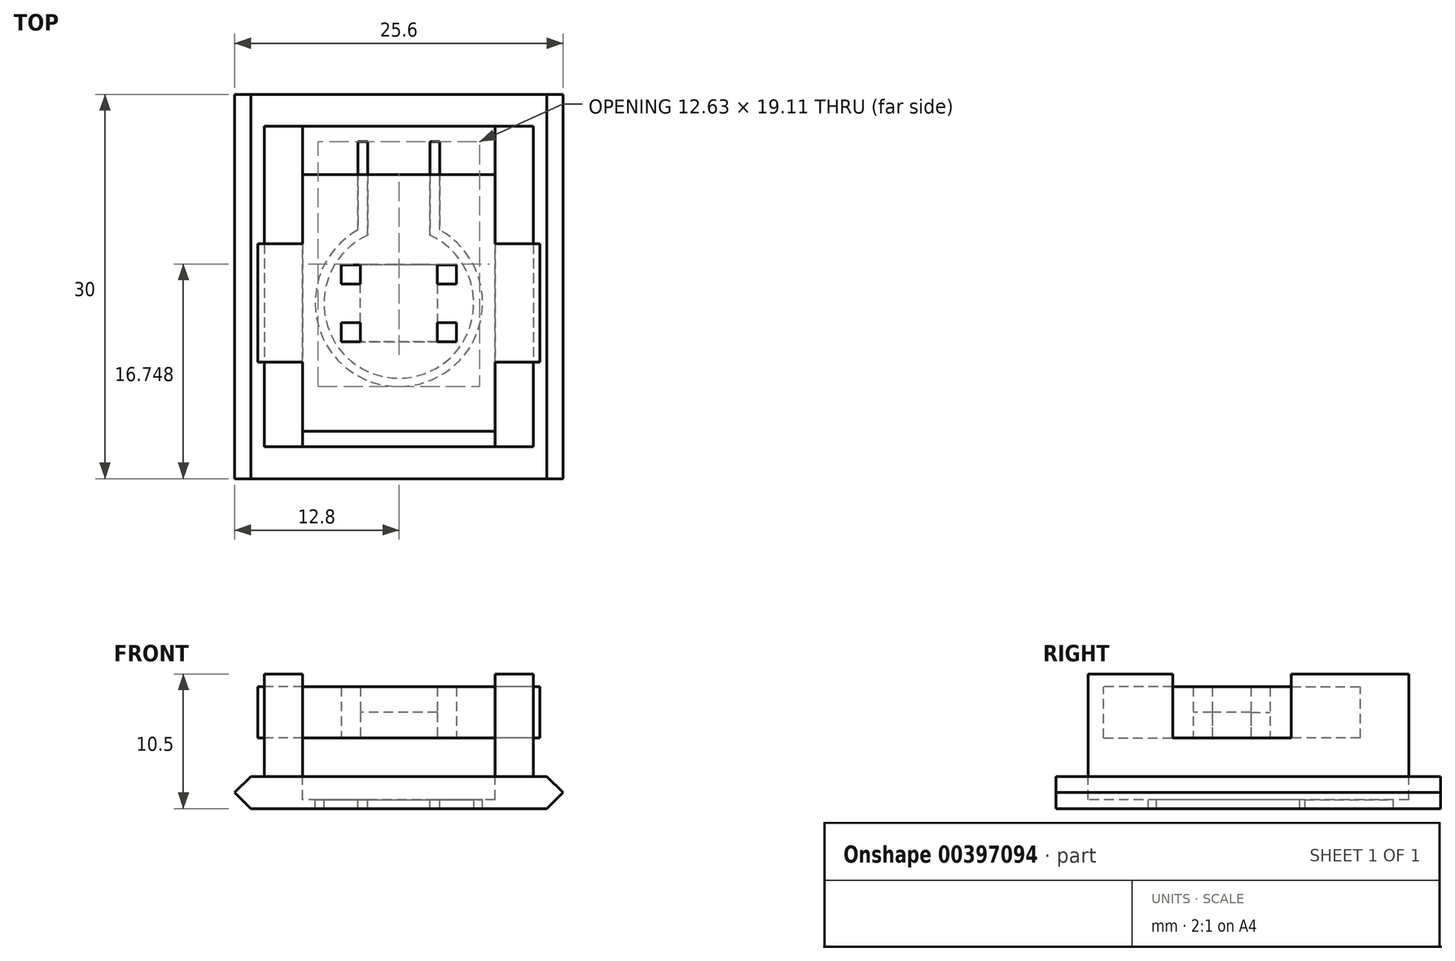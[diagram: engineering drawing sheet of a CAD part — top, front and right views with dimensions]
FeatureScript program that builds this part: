
annotation { "Feature Type Name" : "Feature", "Feature Type Description" : "" }
export const myFeature = defineFeature(function(context is Context, id is Id, definition is map)
    precondition{}
    {
        {
            var Q0;
            Q0=qCreatedBy(makeId("Front.planeOp"),FACE);
            var sketch = newSketch(context, id + "F0", { "sketchPlane" : qUnion([Q0])});
            skLineSegment(sketch, "E0", {"start": v(-11.55, 1.25) * mm, "end": v(11.55, 1.25) * mm});
            skLineSegment(sketch, "E1", {"start": v(11.55, -1.25) * mm, "end": v(-11.55, -1.25) * mm});
            skLineSegment(sketch, "E2", {"start": v(11.55, 1.25) * mm, "end": v(11.55, -1.25) * mm, "construction": true});
            skLineSegment(sketch, "E3", {"start": v(11.55, 1.25) * mm, "end": v(12.8, 0) * mm});
            skLineSegment(sketch, "E4", {"start": v(12.8, 0) * mm, "end": v(11.55, -1.25) * mm});
            skLineSegment(sketch, "E5", {"start": v(-11.55, 1.25) * mm, "end": v(-12.8, 0) * mm});
            skLineSegment(sketch, "E6", {"start": v(-12.8, 0) * mm, "end": v(-11.55, -1.25) * mm});
            skSolve(sketch);
        }
        {
            var Q0;
            Q0=qSketchRegion(id+"F0",true);
            extrude(context, id + "F1", {"entities" : qUnion([Q0]), "depth" : 30 * mm});
        }
        {
            var Q0;
            Q0=makeQuery(id+"F1.opExtrude","SWEPT_FACE",FACE,{"disambiguationData":[OSD([sQuery(id+"F0.wireOp",EDGE,"E0")])]});
            var sketch = newSketch(context, id + "F2", { "sketchPlane" : qUnion([Q0])});
            skLineSegment(sketch, "E7.bottom", {"start": v(7.5, -2.5) * mm, "end": v(-7.5, -2.5) * mm});
            skLineSegment(sketch, "E7.top", {"start": v(7.5, -27.5) * mm, "end": v(-7.5, -27.5) * mm});
            skLineSegment(sketch, "E7.left", {"start": v(7.5, -2.5) * mm, "end": v(7.5, -27.5) * mm});
            skLineSegment(sketch, "E7.right", {"start": v(-7.5, -2.5) * mm, "end": v(-7.5, -27.5) * mm});
            skPoint(sketch, "E7.middle", {"position": v(0, -15) * mm});
            skLineSegment(sketch, "E8", {"start": v(0, 0) * mm, "end": v(0, -30) * mm, "construction": true});
            skSolve(sketch);
        }
        {
            var Q0;
            Q0=qSketchRegion(id+"F2",true);
            extrude(context, id + "F3", {"entities" : qUnion([Q0]), "operationType" : NewBodyOperationType.REMOVE, "oppositeDirection" : true, "depth" : 1.8 * mm});
        }
        {
            var Q0;
            Q0=makeQuery(id+"F3.boolean.opBoolean","COPY",FACE,{"derivedFrom":makeQuery(id+"F3.opExtrude","CAP_FACE",FACE,{"disambiguationData":[OSD([sQuery(id+"F2.wireOp",EDGE,"E7.bottom"),sQuery(id+"F2.wireOp",EDGE,"E7.top"),sQuery(id+"F2.wireOp",EDGE,"E7.left"),sQuery(id+"F2.wireOp",EDGE,"E7.right")])],"isStart":false})});
            var sketch = newSketch(context, id + "F4", { "sketchPlane" : qUnion([Q0])});
            skLineSegment(sketch, "E9", {"start": v(-3.2, -10.59) * mm, "end": v(-3.2, -3.7) * mm});
            skLineSegment(sketch, "E10", {"start": v(-3.2, -3.7) * mm, "end": v(-2.43, -3.7) * mm});
            skLineSegment(sketch, "E11", {"start": v(-2.43, -3.7) * mm, "end": v(-2.43, -11) * mm});
            skLineSegment(sketch, "E12", {"start": v(0, -2.5) * mm, "end": v(0, -27.5) * mm, "construction": true});
            skLineSegment(sketch, "E13.MirrorCS", {"start": v(2.43, -3.7) * mm, "end": v(2.43, -11) * mm});
            skLineSegment(sketch, "E14.MirrorCS", {"start": v(3.2, -3.7) * mm, "end": v(2.43, -3.7) * mm});
            skLineSegment(sketch, "E15.MirrorCS", {"start": v(3.2, -10.59) * mm, "end": v(3.2, -3.7) * mm});
            skArc(sketch, "E16", {"start": v(-3.2, -10.59) * mm, "mid": v(0, -22.8) * mm, "end": v(3.2, -10.59) * mm});
            skArc(sketch, "E17", {"start": v(-2.43, -11) * mm, "mid": v(0, -22.15) * mm, "end": v(2.43, -11) * mm});
            skSolve(sketch);
        }
        {
            var Q0;
            Q0=qSketchRegion(id+"F4",true);
            extrude(context, id + "F5", {"entities" : qUnion([Q0]), "operationType" : NewBodyOperationType.REMOVE, "oppositeDirection" : true, "depth" : 25 * mm});
        }
        {
            var Q0;
            Q0=makeQuery(id+"F1.opExtrude","SWEPT_FACE",FACE,{"disambiguationData":[OSD([sQuery(id+"F0.wireOp",EDGE,"E0")])]});
            var sketch = newSketch(context, id + "F6", { "sketchPlane" : qUnion([Q0])});
            skLineSegment(sketch, "E18.bottom", {"start": v(-7.5, -2.5) * mm, "end": v(-10.5, -2.5) * mm});
            skLineSegment(sketch, "E18.top", {"start": v(-7.5, -27.5) * mm, "end": v(-10.5, -27.5) * mm});
            skLineSegment(sketch, "E18.left", {"start": v(-7.5, -2.5) * mm, "end": v(-7.5, -27.5) * mm});
            skLineSegment(sketch, "E18.right", {"start": v(-10.5, -2.5) * mm, "end": v(-10.5, -27.5) * mm});
            skLineSegment(sketch, "E19.bottom", {"start": v(7.5, -2.5) * mm, "end": v(10.5, -2.5) * mm});
            skLineSegment(sketch, "E19.top", {"start": v(7.5, -27.5) * mm, "end": v(10.5, -27.5) * mm});
            skLineSegment(sketch, "E19.left", {"start": v(7.5, -2.5) * mm, "end": v(7.5, -27.5) * mm});
            skLineSegment(sketch, "E19.right", {"start": v(10.5, -2.5) * mm, "end": v(10.5, -27.5) * mm});
            skSolve(sketch);
        }
        {
            var Q0;
            Q0=qSketchRegion(id+"F6",true);
            extrude(context, id + "F7", {"entities" : qUnion([Q0]), "operationType" : NewBodyOperationType.ADD, "depth" : 8 * mm});
        }
        {
            var Q0;
            Q0=makeQuery(id+"F7.opExtrude","CAP_FACE",FACE,{"disambiguationData":[OSD([sQuery(id+"F6.wireOp",EDGE,"E18.bottom"),sQuery(id+"F6.wireOp",EDGE,"E18.top"),sQuery(id+"F6.wireOp",EDGE,"E18.left"),sQuery(id+"F6.wireOp",EDGE,"E18.right")])],"isStart":false});
            var sketch = newSketch(context, id + "F8", { "sketchPlane" : qUnion([Q0])});
            skPoint(sketch, "E20.0", {"position": v(0, -27.5) * mm});
            skPoint(sketch, "E21.0", {"position": v(0, -2.5) * mm});
            skPoint(sketch, "E22.0", {"position": v(-7.5, -15) * mm});
            skArc(sketch, "E23.0", {"start": v(-3.2, -10.59) * mm, "mid": v(0, -22.8) * mm, "end": v(3.2, -10.59) * mm, "construction": true});
            skLineSegment(sketch, "E24.bottom", {"start": v(11, -20.9) * mm, "end": v(-11, -20.9) * mm});
            skLineSegment(sketch, "E24.top", {"start": v(11, -11.66) * mm, "end": v(-11, -11.66) * mm});
            skLineSegment(sketch, "E24.left", {"start": v(11, -20.9) * mm, "end": v(11, -11.66) * mm});
            skLineSegment(sketch, "E24.right", {"start": v(-11, -20.9) * mm, "end": v(-11, -11.66) * mm});
            skLineSegment(sketch, "E25.0", {"start": v(7.5, -2.5) * mm, "end": v(7.5, -27.5) * mm, "construction": true});
            skLineSegment(sketch, "E26.0", {"start": v(-7.5, -2.5) * mm, "end": v(-7.5, -27.5) * mm, "construction": true});
            skLineSegment(sketch, "E27.bottom", {"start": v(7.5, -26.3) * mm, "end": v(-7.5, -26.3) * mm});
            skLineSegment(sketch, "E27.top", {"start": v(7.5, -6.26) * mm, "end": v(-7.5, -6.26) * mm});
            skLineSegment(sketch, "E27.left", {"start": v(7.5, -26.3) * mm, "end": v(7.5, -6.26) * mm});
            skLineSegment(sketch, "E27.right", {"start": v(-7.5, -26.3) * mm, "end": v(-7.5, -6.26) * mm});
            skSolve(sketch);
        }
        {
            var Q0;
            Q0=qSketchRegion(id+"F8",true);
            extrude(context, id + "F9", {"entities" : qUnion([Q0]), "operationType" : NewBodyOperationType.REMOVE, "oppositeDirection" : true, "depth" : 5 * mm});
        }
        {
            var Q0;
            Q0=qSketchRegion(id+"F8",true);
            extrude(context, id + "F10", {"entities" : qUnion([Q0]), "oppositeDirection" : true, "depth" : 5 * mm});
        }
        {
            var Q0;
            Q0=qSketchRegion(id+"F8",true);
            extrude(context, id + "F11", {"entities" : qUnion([Q0]), "operationType" : NewBodyOperationType.REMOVE, "oppositeDirection" : true, "depth" : 1 * mm});
        }
        {
            var Q0;
            Q0=makeQuery(id+"F10.opExtrude","CAP_FACE",FACE,{"disambiguationData":[OSD([sQuery(id+"F8.wireOp",EDGE,"E24.bottom"),sQuery(id+"F8.wireOp",EDGE,"E24.top"),sQuery(id+"F8.wireOp",EDGE,"E24.left"),sQuery(id+"F8.wireOp",EDGE,"E24.right"),sQuery(id+"F8.wireOp",EDGE,"E27.bottom"),sQuery(id+"F8.wireOp",EDGE,"E27.top"),sQuery(id+"F8.wireOp",EDGE,"E27.left"),sQuery(id+"F8.wireOp",EDGE,"E27.right")])],"isStart":false});
            var sketch = newSketch(context, id + "F12", { "sketchPlane" : qUnion([Q0])});
            skArc(sketch, "E28.0", {"start": v(2.43, 11) * mm, "mid": v(0, 22.15) * mm, "end": v(-2.43, 11) * mm, "construction": true});
            skLineSegment(sketch, "E29.bottom", {"start": v(-3, 19.31) * mm, "end": v(-4.5, 19.31) * mm});
            skLineSegment(sketch, "E29.top", {"start": v(-3, 17.81) * mm, "end": v(-4.5, 17.81) * mm});
            skLineSegment(sketch, "E29.left", {"start": v(-3, 19.31) * mm, "end": v(-3, 17.81) * mm});
            skLineSegment(sketch, "E29.right", {"start": v(-4.5, 19.31) * mm, "end": v(-4.5, 17.81) * mm});
            skLineSegment(sketch, "E30.MirrorCS", {"start": v(3, 17.81) * mm, "end": v(4.5, 17.81) * mm});
            skLineSegment(sketch, "E31.MirrorCS", {"start": v(4.5, 19.31) * mm, "end": v(4.5, 17.81) * mm});
            skLineSegment(sketch, "E32.MirrorCS", {"start": v(3, 19.31) * mm, "end": v(4.5, 19.31) * mm});
            skLineSegment(sketch, "E33.MirrorCS", {"start": v(3, 19.31) * mm, "end": v(3, 17.81) * mm});
            skLineSegment(sketch, "E34", {"start": v(-10.51, 16.31) * mm, "end": v(11.29, 16.31) * mm, "construction": true});
            skPoint(sketch, "E34.endSnap0", {"position": v(3, 16.31) * mm});
            skLineSegment(sketch, "E35.MirrorCS", {"start": v(3, 14.81) * mm, "end": v(4.5, 14.81) * mm});
            skLineSegment(sketch, "E36.MirrorCS", {"start": v(4.5, 13.31) * mm, "end": v(4.5, 14.81) * mm});
            skLineSegment(sketch, "E37.MirrorCS", {"start": v(3, 13.31) * mm, "end": v(3, 14.81) * mm});
            skLineSegment(sketch, "E38.MirrorCS", {"start": v(3, 13.31) * mm, "end": v(4.5, 13.31) * mm});
            skLineSegment(sketch, "E39.MirrorCS", {"start": v(-3, 14.81) * mm, "end": v(-4.5, 14.81) * mm});
            skLineSegment(sketch, "E40.MirrorCS", {"start": v(-3, 13.31) * mm, "end": v(-3, 14.81) * mm});
            skLineSegment(sketch, "E41.MirrorCS", {"start": v(-3, 13.31) * mm, "end": v(-4.5, 13.31) * mm});
            skLineSegment(sketch, "E42.MirrorCS", {"start": v(-4.5, 13.31) * mm, "end": v(-4.5, 14.81) * mm});
            skSolve(sketch);
        }
        {
            var Q0;
            Q0=qSketchRegion(id+"F12",true);
            extrude(context, id + "F13", {"entities" : qUnion([Q0]), "operationType" : NewBodyOperationType.REMOVE, "oppositeDirection" : true, "depth" : 25 * mm});
        }
        {
            var Q0;
            Q0=makeQuery(id+"F10.opExtrude","CAP_FACE",FACE,{"disambiguationData":[OSD([sQuery(id+"F8.wireOp",EDGE,"E24.bottom"),sQuery(id+"F8.wireOp",EDGE,"E24.top"),sQuery(id+"F8.wireOp",EDGE,"E24.left"),sQuery(id+"F8.wireOp",EDGE,"E24.right"),sQuery(id+"F8.wireOp",EDGE,"E27.bottom"),sQuery(id+"F8.wireOp",EDGE,"E27.top"),sQuery(id+"F8.wireOp",EDGE,"E27.left"),sQuery(id+"F8.wireOp",EDGE,"E27.right")])],"isStart":false});
            var sketch = newSketch(context, id + "F14", { "sketchPlane" : qUnion([Q0])});
            skArc(sketch, "E43.0", {"start": v(-2.43, 11) * mm, "mid": v(0, 22.15) * mm, "end": v(2.43, 11) * mm, "construction": true});
            skLineSegment(sketch, "E44.bottom", {"start": v(3, 13.31) * mm, "end": v(-3, 13.31) * mm});
            skLineSegment(sketch, "E44.top", {"start": v(3, 19.31) * mm, "end": v(-3, 19.31) * mm});
            skLineSegment(sketch, "E44.left", {"start": v(3, 13.31) * mm, "end": v(3, 19.31) * mm});
            skLineSegment(sketch, "E44.right", {"start": v(-3, 13.31) * mm, "end": v(-3, 19.31) * mm});
            skSolve(sketch);
        }
        {
            var Q0;
            Q0=qSketchRegion(id+"F14",true);
            extrude(context, id + "F15", {"entities" : qUnion([Q0]), "operationType" : NewBodyOperationType.REMOVE, "oppositeDirection" : true, "depth" : 2 * mm});
        }
    });
